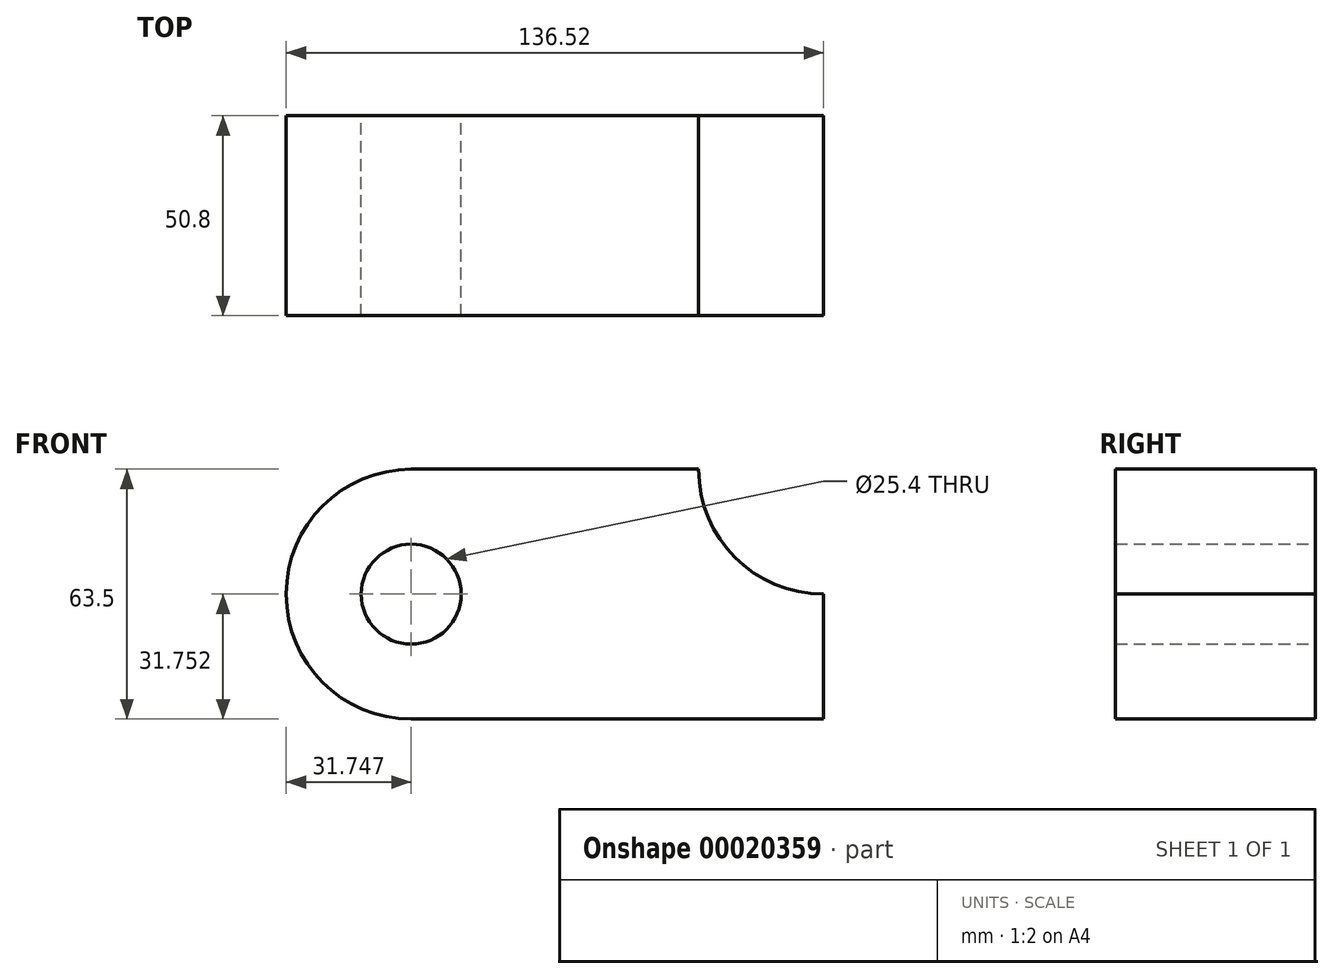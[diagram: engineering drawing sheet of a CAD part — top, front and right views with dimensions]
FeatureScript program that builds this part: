
annotation { "Feature Type Name" : "Feature", "Feature Type Description" : "" }
export const myFeature = defineFeature(function(context is Context, id is Id, definition is map)
    precondition{}
    {
        {
            var Q0;
            Q0=qCreatedBy(makeId("Front.planeOp"),FACE);
            var sketch = newSketch(context, id + "F0", { "sketchPlane" : qUnion([Q0])});
            skLineSegment(sketch, "E0.bottom", {"start": v(-61.28, 35.42) * mm, "end": v(11.74, 35.42) * mm});
            skLineSegment(sketch, "E0.top", {"start": v(-61.28, -28.08) * mm, "end": v(43.5, -28.08) * mm});
            skLineSegment(sketch, "E0.right", {"start": v(43.5, 3.67) * mm, "end": v(43.5, -28.08) * mm});
            skArc(sketch, "E1", {"start": v(-61.28, 35.42) * mm, "mid": v(-93.03, 3.67) * mm, "end": v(-61.28, -28.08) * mm});
            skPoint(sketch, "E2.trimOffspring.start.orphan", {"position": v(-8.9, 3.67) * mm});
            skCircle(sketch, "E3", {"center": v(-61.28, 3.67) * mm, "radius": 12.7 * mm});
            skArc(sketch, "E4", {"start": v(11.74, 35.42) * mm, "mid": v(21.04, 12.97) * mm, "end": v(43.5, 3.67) * mm});
            skSolve(sketch);
        }
        {
            var Q0;
            Q0=makeQuery(id+"F0.imprint","IMPRINT",FACE,{"disambiguationData":[TD([[makeQuery(id+"F0.imprint","IMPRINT",EDGE,{"derivedFrom":sQuery(id+"F0.wireOp",EDGE,"E0.bottom")}),-1.0]])]});
            extrude(context, id + "F1", {"entities" : qUnion([Q0]), "depth" : 50.8 * mm});
        }
    });
